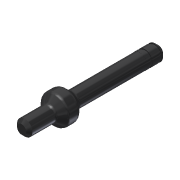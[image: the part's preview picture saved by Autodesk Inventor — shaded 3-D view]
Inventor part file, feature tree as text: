
AUTODESK INVENTOR PART (.ipt)
format: ipt  version: 2013 (Build 170138000, 138)  size: 117,248 bytes
history: native  units: in
note: dims shown in document units (in); Inventor stores cm internally (conversion verified against a paired STEP export)
features: chamfer x1, other x1, imported_body x1
ambient origin geometry x8: Origin, YZ Plane, XZ Plane, XY Plane, X Axis, Y Axis, Z Axis, Center Point
feature tree (3):
  chamfer  "Chamfer1"  [1 undecoded]
  other  "217-2790-004 Rev21"
  imported_body  "Base1"
note: 1 required parameter value undecoded (feature->parameter linkage not recoverable at this tier; creation-order binding heuristic only, values carry confidence <= 0.55)
